# Revit family: Deca_Acabamento para registro de gaveta até ½''_Wish_4900.WSH.PQ
name_source: partatom
category: Plumbing Fixtures
units: mm (PartAtom-declared; Revit-internal decimal feet)

## family parameters
Cut with Voids When Loaded = No
Host = Face
Part Type = Normal
Room Calculation Point = No
Round Connector Dimension = Use Diameter
Shared = No

## types (2) — shared parameters
Aprovado por = quattroD
Atendimento ao Cliente = 0800-0117073
Categoria = Metais para banheiro
Composição Básica = Liga de Cobre (bronze e latão);Plásticos de Engenharia
Consumo = Não Possui
Criado por = quattroD
Código Pai = 4900.WSH.PQ
Default Elevation = 1.8 m
Linha = Deca Wish
Manufacturer = DECA
Norma = Não Possui
Peso Líquido (Kg) = 0.227
Segmento = Banheiro Luxo (D43)
Tipo de rosca de entrada = BSP NBR 8133
URL = www.deca.com.br

## per-type parameters (varying)
| type | Cor Principal | Cor Secundária | Material | Model | Tipo de dispositivo economizador | Tipo de mecanismo utilizado |
| 4900.C.WSH.PQ_Cromado | Cromado | Branco | Deca_Cromado | 4900.C.WSH.PQ | Não | MVC -1/4 volta |
| 4900.GL.WSH.PQ.RD_Red Gold | Red Gold |  | Deca_Red Gold | 4900.GL.WSH.PQ.RD | Sim | MVC - 1/2 volta |

## geometry (parser evidence)
native form markers: Sweep x1
no freeform markers — native parametric forms only
